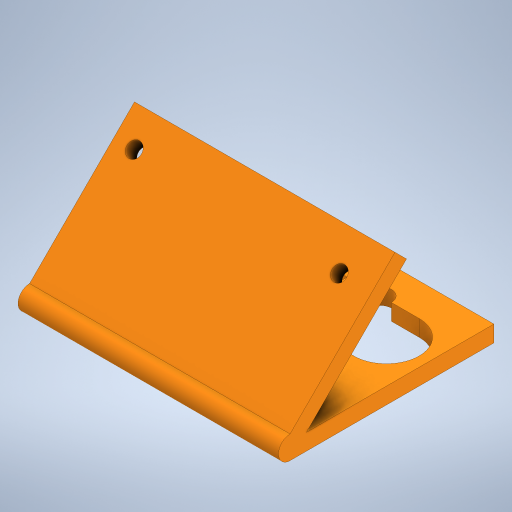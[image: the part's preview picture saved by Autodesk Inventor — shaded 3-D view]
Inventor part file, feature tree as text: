
AUTODESK INVENTOR PART (.ipt)
format: ipt  version: 2023 (Build 270158000, 158)  size: 334,336 bytes
history: native  units: mm
features: extrude x5, sketch x5
ambient origin geometry x8: Origin, YZ Plane, XZ Plane, XY Plane, X Axis, Y Axis, Z Axis, Center Point
bodies: Solid1 (feature_tree)
feature tree (10):
  extrude  "Extrusion1"  Depth=20.0mm
  extrude  "Extrusion2"  Depth=21.0mm
  extrude  "Extrusion3"  Depth=12.5mm
  extrude  "Extrusion4"  Depth=2.5mm
  extrude  "Extrusion5"  Depth=2.5mm
  sketch  "Sketch1"  dims[d0=20.0mm d1=20.0mm]
  sketch  "Sketch2"  dims[d2=54.0mm d3=21.0mm]
  sketch  "Sketch3"  dims[d4=12.5mm d5=12.5mm]
  sketch  "Sketch4"  dims[d6=21.0mm d7=2.5mm]
  sketch  "Sketch5"  dims[d8=2.5mm d9=2.5mm d10=2.5mm d11=5.0mm d12=5.0mm d13=5.0mm d14=5.0mm d15=11.0mm d16=11.0mm d17=40.0mm d18=80.0mm d19=13.0mm d20=20.0mm d21=5.0mm d22=0.0mm d23=45.0deg d24=5.0mm d25=5.0mm d26=80.0mm d27=0.0mm d28=30.0mm d29=10.0mm d30=25.0mm d31=10.0mm d32=80.0mm d33=0.0mm d34=10.0mm d35=10.0mm d36=4.5mm d37=10.0mm d38=10.0mm d39=4.5mm d40=80.0mm d41=0.0mm d42=7.0mm d43=7.0mm d44=7.0mm d45=7.0mm d46=20.0mm d47=0.0mm d48=20.0mm d49=0.0mm d50=6.0mm d51=0.0mm]
